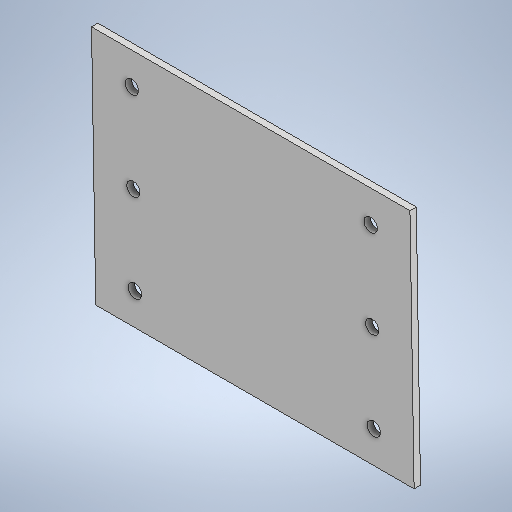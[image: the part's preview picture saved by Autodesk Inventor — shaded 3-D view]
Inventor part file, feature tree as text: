
AUTODESK INVENTOR PART (.ipt)
format: ipt  version: 2025 (Build 290162010, 162A)  size: 255,488 bytes
history: native  units: mm
features: other x2, sheet_metal_op x1, sketch x1
ambient origin geometry x8: Origin, YZ Plane, XZ Plane, XY Plane, X Axis, Y Axis, Z Axis, Center Point
bodies: Body1 (feature_tree)
feature tree (4):
  sheet_metal_op  "Face2"
  sketch  "Sketch5"  dims[d26=400.0mm d27=0.174533mm d28=400.0mm d29=300.0mm d30=8.0mm d31=50.0mm d33=40.0mm d34=40.0mm d35=17.0mm]
  other  "Plate3"
  other  "Definition1"
